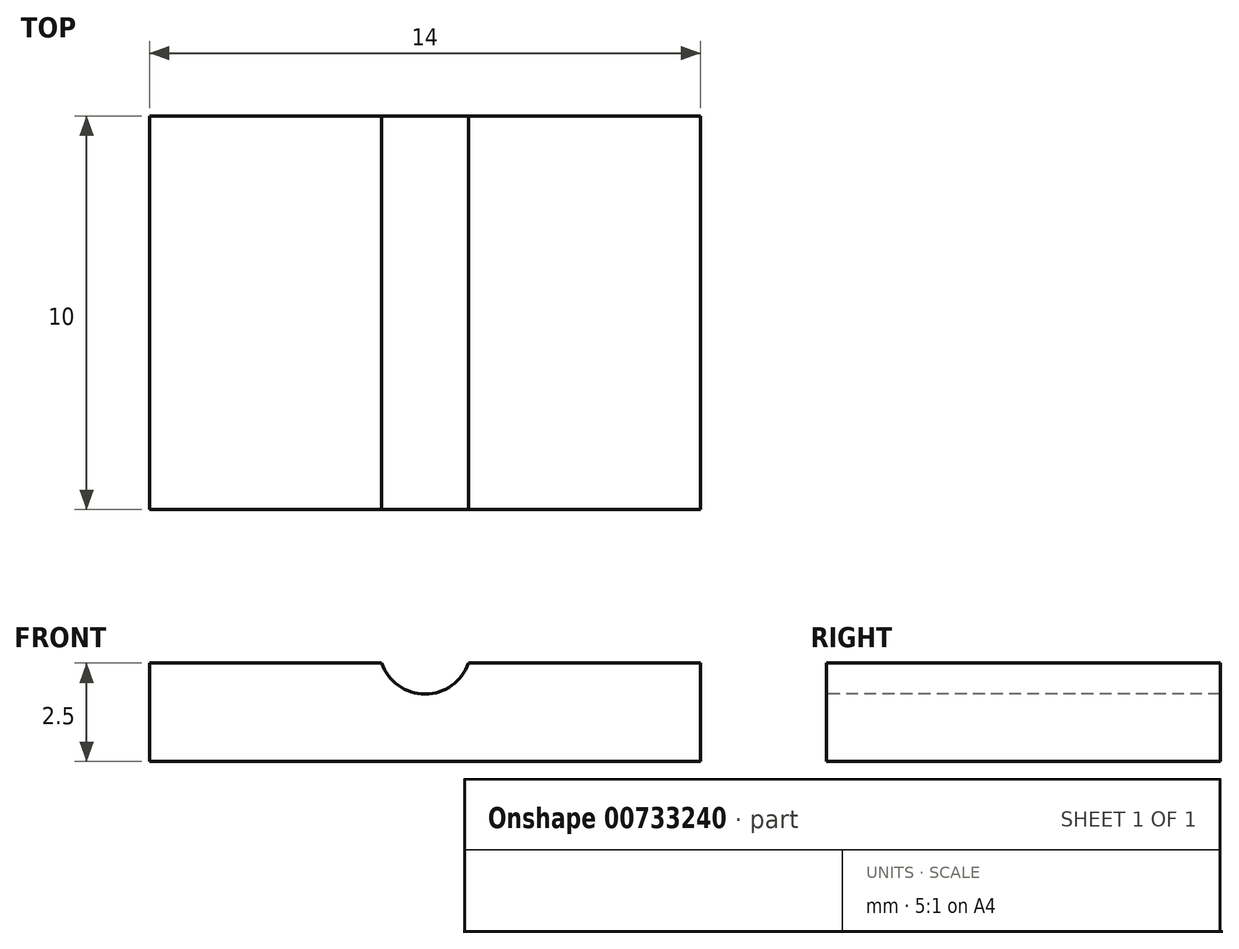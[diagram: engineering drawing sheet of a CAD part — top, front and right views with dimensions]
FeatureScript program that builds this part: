
annotation { "Feature Type Name" : "Feature", "Feature Type Description" : "" }
export const myFeature = defineFeature(function(context is Context, id is Id, definition is map)
    precondition{}
    {
        {
            var Q0;
            Q0=qCreatedBy(makeId("Top.planeOp"),FACE);
            var sketch = newSketch(context, id + "F0", { "sketchPlane" : qUnion([Q0])});
            skLineSegment(sketch, "E0.bottom", {"start": v(-7, 5) * mm, "end": v(7, 5) * mm});
            skLineSegment(sketch, "E0.top", {"start": v(-7, -5) * mm, "end": v(7, -5) * mm});
            skLineSegment(sketch, "E0.left", {"start": v(-7, 5) * mm, "end": v(-7, -5) * mm});
            skLineSegment(sketch, "E0.right", {"start": v(7, 5) * mm, "end": v(7, -5) * mm});
            skPoint(sketch, "E0.middle", {"position": v(0, 0) * mm});
            skSolve(sketch);
        }
        {
            var Q0;
            Q0=makeQuery(id+"F0.imprint","IMPRINT",FACE,{"disambiguationData":[TD([[makeQuery(id+"F0.imprint","IMPRINT",EDGE,{"derivedFrom":sQuery(id+"F0.wireOp",EDGE,"E0.bottom")}),-1.0]])]});
            extrude(context, id + "F1", {"entities" : qUnion([Q0]), "depth" : 2.5 * mm, "offsetDistance" : 25 * mm});
        }
        {
            var Q0;
            Q0=makeQuery(id+"F1.opExtrude","SWEPT_FACE",FACE,{"disambiguationData":[OSD([sQuery(id+"F0.wireOp",EDGE,"E0.top")])]});
            var sketch = newSketch(context, id + "F2", { "sketchPlane" : qUnion([Q0])});
            skCircle(sketch, "E1", {"center": v(0, 2.5) * mm, "radius": 1.1 * mm, "construction": true});
            skArc(sketch, "E2", {"start": v(-1.1, 2.5) * mm, "mid": v(0, 1.71) * mm, "end": v(1.1, 2.5) * mm});
            skSolve(sketch);
        }
        {
            var Q0;
            {var subQ0=sQuery(id+"F2.wireOp",EDGE,"E2");Q0=makeQuery(id+"F2.imprint","IMPRINT",FACE,{"disambiguationData":[TD([[makeQuery(id+"F2.imprint","IMPRINT",EDGE,{"derivedFrom":subQ0}),1.0]])]});}
            extrude(context, id + "F3", {"entities" : qUnion([Q0]), "operationType" : NewBodyOperationType.REMOVE, "endBound" : BoundingType.THROUGH_ALL, "oppositeDirection" : true, "depth" : 25 * mm, "offsetDistance" : 25 * mm});
        }
    });
